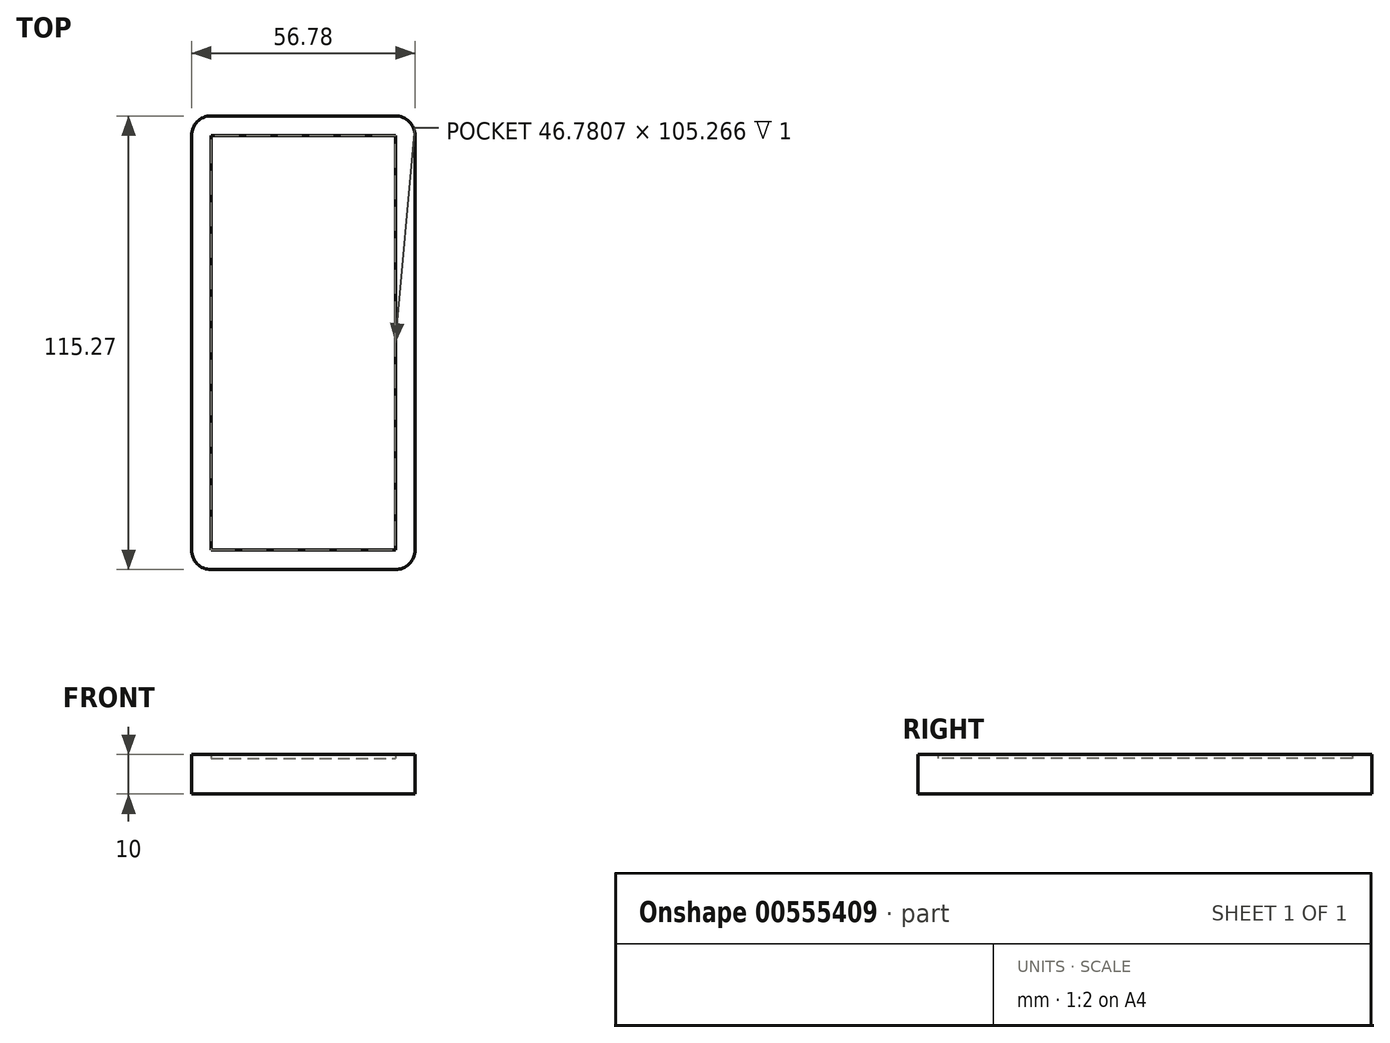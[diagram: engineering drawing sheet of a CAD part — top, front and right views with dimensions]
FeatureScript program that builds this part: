
annotation { "Feature Type Name" : "Feature", "Feature Type Description" : "" }
export const myFeature = defineFeature(function(context is Context, id is Id, definition is map)
    precondition{}
    {
        {
            var Q0;
            Q0=qCreatedBy(makeId("Top.planeOp"),FACE);
            var sketch = newSketch(context, id + "F0", { "sketchPlane" : qUnion([Q0])});
            skLineSegment(sketch, "E0.bottom", {"start": v(-27.68, 57.52) * mm, "end": v(19.1, 57.52) * mm});
            skLineSegment(sketch, "E0.top", {"start": v(-27.68, -57.75) * mm, "end": v(19.1, -57.75) * mm});
            skLineSegment(sketch, "E0.left", {"start": v(-32.68, 52.52) * mm, "end": v(-32.68, -52.75) * mm});
            skLineSegment(sketch, "E0.right", {"start": v(24.1, 52.52) * mm, "end": v(24.1, -52.75) * mm});
            skPoint(sketch, "E1.visualSharp", {"position": v(-32.68, 57.52) * mm});
            skArc(sketch, "E1.filletArc", {"start": v(-27.68, 57.52) * mm, "mid": v(-31.22, 56.05) * mm, "end": v(-32.68, 52.52) * mm});
            skPoint(sketch, "E2.visualSharp", {"position": v(24.1, 57.52) * mm});
            skArc(sketch, "E2.filletArc", {"start": v(24.1, 52.52) * mm, "mid": v(22.63, 56.05) * mm, "end": v(19.1, 57.52) * mm});
            skPoint(sketch, "E3.visualSharp", {"position": v(-32.68, -57.75) * mm});
            skArc(sketch, "E3.filletArc", {"start": v(-32.68, -52.75) * mm, "mid": v(-31.22, -56.28) * mm, "end": v(-27.68, -57.75) * mm});
            skPoint(sketch, "E4.visualSharp", {"position": v(24.1, -57.75) * mm});
            skArc(sketch, "E4.filletArc", {"start": v(19.1, -57.75) * mm, "mid": v(22.63, -56.28) * mm, "end": v(24.1, -52.75) * mm});
            skSolve(sketch);
        }
        {
            var Q0;
            Q0=makeQuery(id+"F0.imprint","IMPRINT",FACE,{"disambiguationData":[TD([[makeQuery(id+"F0.imprint","IMPRINT",EDGE,{"derivedFrom":sQuery(id+"F0.wireOp",EDGE,"E0.bottom")}),-1.0]])]});
            extrude(context, id + "F1", {"entities" : qUnion([Q0]), "depth" : 7 * mm, "offsetDistance" : 25 * mm});
        }
        {
            var Q0;
            Q0=makeQuery(id+"F1.opExtrude","CAP_FACE",FACE,{"disambiguationData":[OSD([sQuery(id+"F0.wireOp",EDGE,"E0.bottom"),sQuery(id+"F0.wireOp",EDGE,"E0.top"),sQuery(id+"F0.wireOp",EDGE,"E0.left"),sQuery(id+"F0.wireOp",EDGE,"E0.right"),sQuery(id+"F0.wireOp",EDGE,"E1.filletArc"),sQuery(id+"F0.wireOp",EDGE,"E2.filletArc"),sQuery(id+"F0.wireOp",EDGE,"E3.filletArc"),sQuery(id+"F0.wireOp",EDGE,"E4.filletArc")])],"isStart":false});
            var sketch = newSketch(context, id + "F2", { "sketchPlane" : qUnion([Q0])});
            skLineSegment(sketch, "E5.bottom", {"start": v(-27.68, 52.52) * mm, "end": v(19.1, 52.52) * mm});
            skLineSegment(sketch, "E5.top", {"start": v(-27.68, -52.75) * mm, "end": v(19.1, -52.75) * mm});
            skLineSegment(sketch, "E5.left", {"start": v(-27.68, 52.52) * mm, "end": v(-27.68, -52.75) * mm});
            skLineSegment(sketch, "E5.right", {"start": v(19.1, 52.52) * mm, "end": v(19.1, -52.75) * mm});
            skSolve(sketch);
        }
        {
            var Q0;
            Q0=makeQuery(id+"F2.imprint","IMPRINT",FACE,{"disambiguationData":[TD([[makeQuery(id+"F2.imprint","IMPRINT",EDGE,{"derivedFrom":sQuery(id+"F2.wireOp",EDGE,"E5.bottom")}),-1.0]])]});
            extrude(context, id + "F3", {"entities" : qUnion([Q0]), "operationType" : NewBodyOperationType.ADD, "depth" : 2 * mm, "offsetDistance" : 25 * mm});
        }
        {
            var Q0;
            Q0=makeQuery(id+"F1.opExtrude","CAP_FACE",FACE,{"disambiguationData":[OSD([sQuery(id+"F0.wireOp",EDGE,"E0.bottom"),sQuery(id+"F0.wireOp",EDGE,"E0.top"),sQuery(id+"F0.wireOp",EDGE,"E0.left"),sQuery(id+"F0.wireOp",EDGE,"E0.right"),sQuery(id+"F0.wireOp",EDGE,"E1.filletArc"),sQuery(id+"F0.wireOp",EDGE,"E2.filletArc"),sQuery(id+"F0.wireOp",EDGE,"E3.filletArc"),sQuery(id+"F0.wireOp",EDGE,"E4.filletArc")])],"isStart":false});
            extrude(context, id + "F4", {"entities" : qUnion([Q0]), "operationType" : NewBodyOperationType.ADD, "depth" : 3 * mm, "offsetDistance" : 25 * mm});
        }
    });
